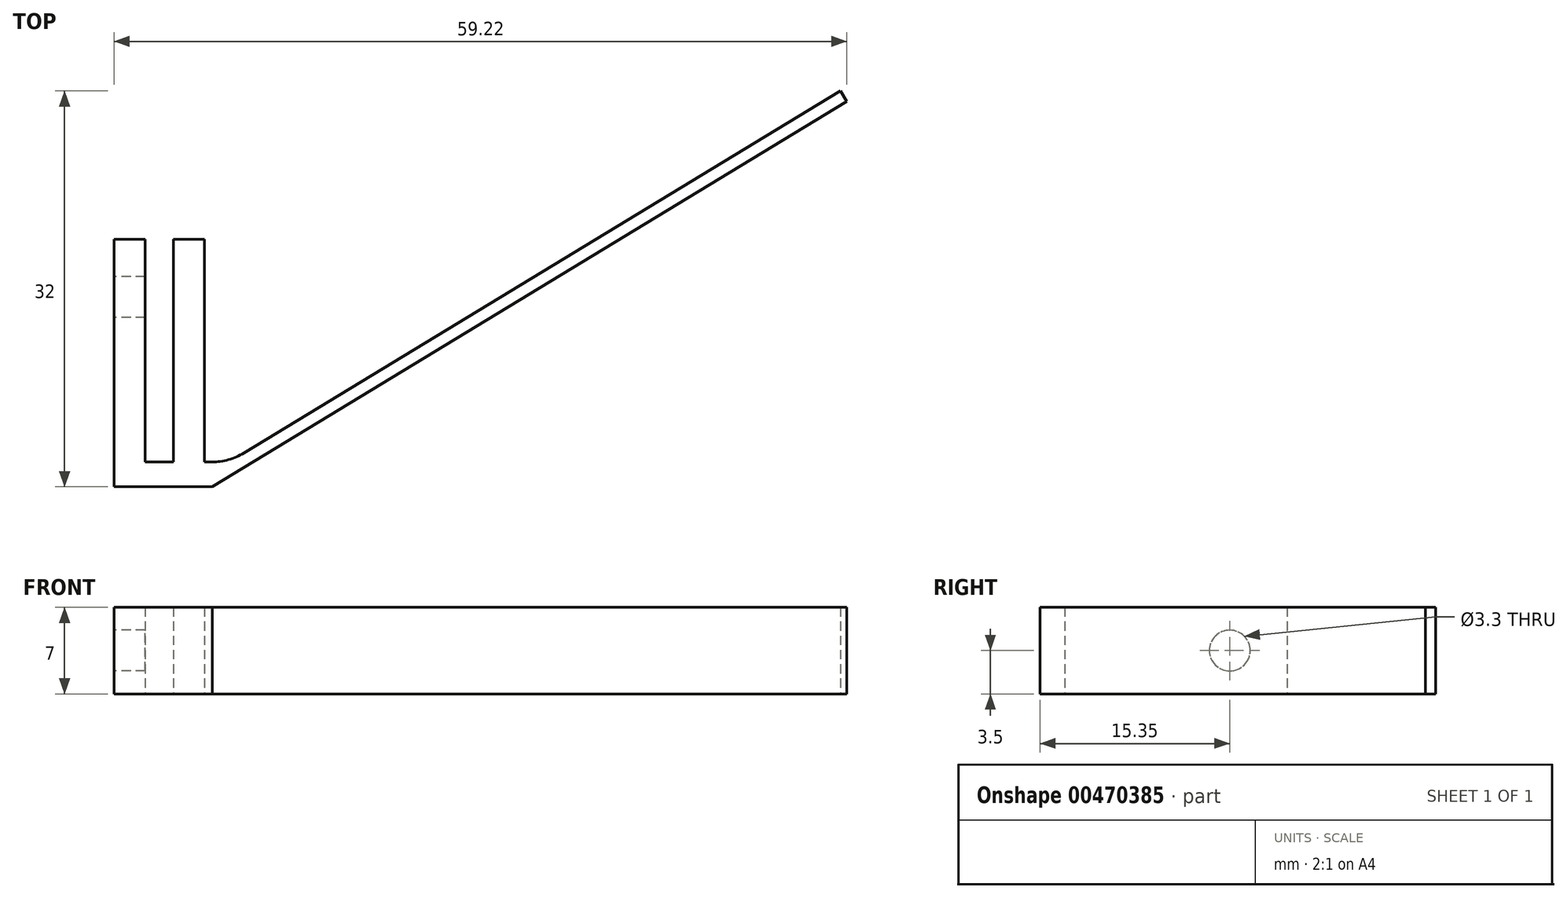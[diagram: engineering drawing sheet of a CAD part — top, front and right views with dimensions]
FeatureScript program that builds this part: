
annotation { "Feature Type Name" : "Feature", "Feature Type Description" : "" }
export const myFeature = defineFeature(function(context is Context, id is Id, definition is map)
    precondition{}
    {
        {
            var Q0;
            Q0=qCreatedBy(makeId("Top.planeOp"),FACE);
            var sketch = newSketch(context, id + "F0", { "sketchPlane" : qUnion([Q0])});
            skLineSegment(sketch, "E0", {"start": v(0, 0) * mm, "end": v(0, 20) * mm});
            skLineSegment(sketch, "E1", {"start": v(0, 20) * mm, "end": v(2.5, 20) * mm});
            skLineSegment(sketch, "E2", {"start": v(2.5, 20) * mm, "end": v(2.5, 2) * mm});
            skLineSegment(sketch, "E3", {"start": v(2.5, 2) * mm, "end": v(4.8, 2) * mm});
            skLineSegment(sketch, "E4", {"start": v(4.8, 2) * mm, "end": v(4.8, 20) * mm});
            skLineSegment(sketch, "E5", {"start": v(4.8, 20) * mm, "end": v(7.3, 20) * mm});
            skLineSegment(sketch, "E6", {"start": v(7.3, 2) * mm, "end": v(7.3, 20) * mm});
            skLineSegment(sketch, "E7", {"start": v(4.8, 2) * mm, "end": v(7.3, 2) * mm, "construction": true});
            skLineSegment(sketch, "E8", {"start": v(7.3, 2) * mm, "end": v(7.9, 2) * mm});
            skLineSegment(sketch, "E9", {"start": v(10.5, 2.73) * mm, "end": v(58.7, 32) * mm});
            skLineSegment(sketch, "E10", {"start": v(58.7, 32) * mm, "end": v(59.22, 31.15) * mm});
            skLineSegment(sketch, "E11", {"start": v(59.22, 31.15) * mm, "end": v(7.93, 0) * mm});
            skLineSegment(sketch, "E12", {"start": v(0, 0) * mm, "end": v(7.93, 0) * mm});
            skPoint(sketch, "E13.visualSharp", {"position": v(9.3, 2) * mm});
            skArc(sketch, "E13.filletArc", {"start": v(7.9, 2) * mm, "mid": v(9.25, 2.19) * mm, "end": v(10.5, 2.73) * mm});
            skSolve(sketch);
        }
        {
            var Q0;
            Q0=makeQuery(id+"F0.imprint","IMPRINT",FACE,{"disambiguationData":[TD([[makeQuery(id+"F0.imprint","IMPRINT",EDGE,{"derivedFrom":sQuery(id+"F0.wireOp",EDGE,"E0")}),-1.0]])]});
            extrude(context, id + "F1", {"entities" : qUnion([Q0]), "depth" : 7 * mm});
        }
        {
            var Q0;
            Q0=makeQuery(id+"F1.opExtrude","SWEPT_FACE",FACE,{"disambiguationData":[OSD([sQuery(id+"F0.wireOp",EDGE,"E0")])]});
            var sketch = newSketch(context, id + "F2", { "sketchPlane" : qUnion([Q0])});
            skCircle(sketch, "E14", {"center": v(-15.35, 3.5) * mm, "radius": 1.65 * mm});
            skLineSegment(sketch, "E15", {"start": v(-20, 3.5) * mm, "end": v(-15.35, 3.5) * mm, "construction": true});
            skPoint(sketch, "E16", {"position": v(-17, 3.5) * mm});
            skSolve(sketch);
        }
        {
            var Q0;
            Q0=makeQuery(id+"F2.imprint","IMPRINT",FACE,{"disambiguationData":[TD([[makeQuery(id+"F2.imprint","IMPRINT",EDGE,{"derivedFrom":sQuery(id+"F2.wireOp",EDGE,"E14")}),1.0]])]});
            var Q1;
            Q1=makeQuery(id+"F1.opExtrude","SWEPT_FACE",FACE,{"disambiguationData":[OSD([sQuery(id+"F0.wireOp",EDGE,"E2")])]});
            extrude(context, id + "F3", {"entities" : qUnion([Q0]), "operationType" : NewBodyOperationType.REMOVE, "endBound" : BoundingType.UP_TO_SURFACE, "oppositeDirection" : true, "endBoundEntityFace" : qUnion([Q1]), "depth" : 25 * mm});
        }
    });
